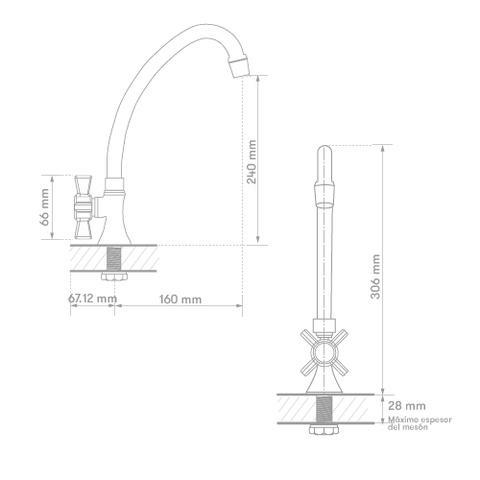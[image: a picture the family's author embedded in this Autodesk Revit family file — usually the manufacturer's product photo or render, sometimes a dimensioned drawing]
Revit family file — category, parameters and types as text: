
# Revit family: II-BR05-11-BRAZO ARCO MÓVIL LAVAPLATOS
name_source: partatom
category: Plumbing Fixtures
revit_build: Autodesk Revit 2018 (Build: 20170223_1515(x64)
units: mm (PartAtom-declared; Revit-internal decimal feet)

## family parameters
Cut with Voids When Loaded = No
Host = Face
OmniClass Number = 23.31.11.00
Part Type = Normal
Room Calculation Point = No
Round Connector Dimension = Use Diameter
Shared = No

## types (1)
- II-BR05-11
    Alto = 235 mm  [stored 0.770997 ft]
    Ancho = 54 mm  [stored 0.177165 ft]
    CW Connection = Yes
    Default Elevation = 0 mm  [stored 0 ft]
    Description = Brazo Griferia Cocina
    HW Connection = Yes
    Manufacturer = Gricol
    Model = II-BR05-11
    Plastico ABS Cromado = Metal Laton Cromado
    Product Name = BRAZO ARCO MÓVIL LAVAPLATOS
    Profundidad = 125 mm
    Type Image = LOGO-01.jpg
    URL = https://www.gricol.com
    Vent Connection = No
    Waste Connection = No

note: [stored X ft] marks values corroborated as IEEE doubles in the binary element streams (Revit-internal decimal feet)

## geometry (parser evidence)
native form markers: Blend x2, Sweep x5
no freeform markers — native parametric forms only
